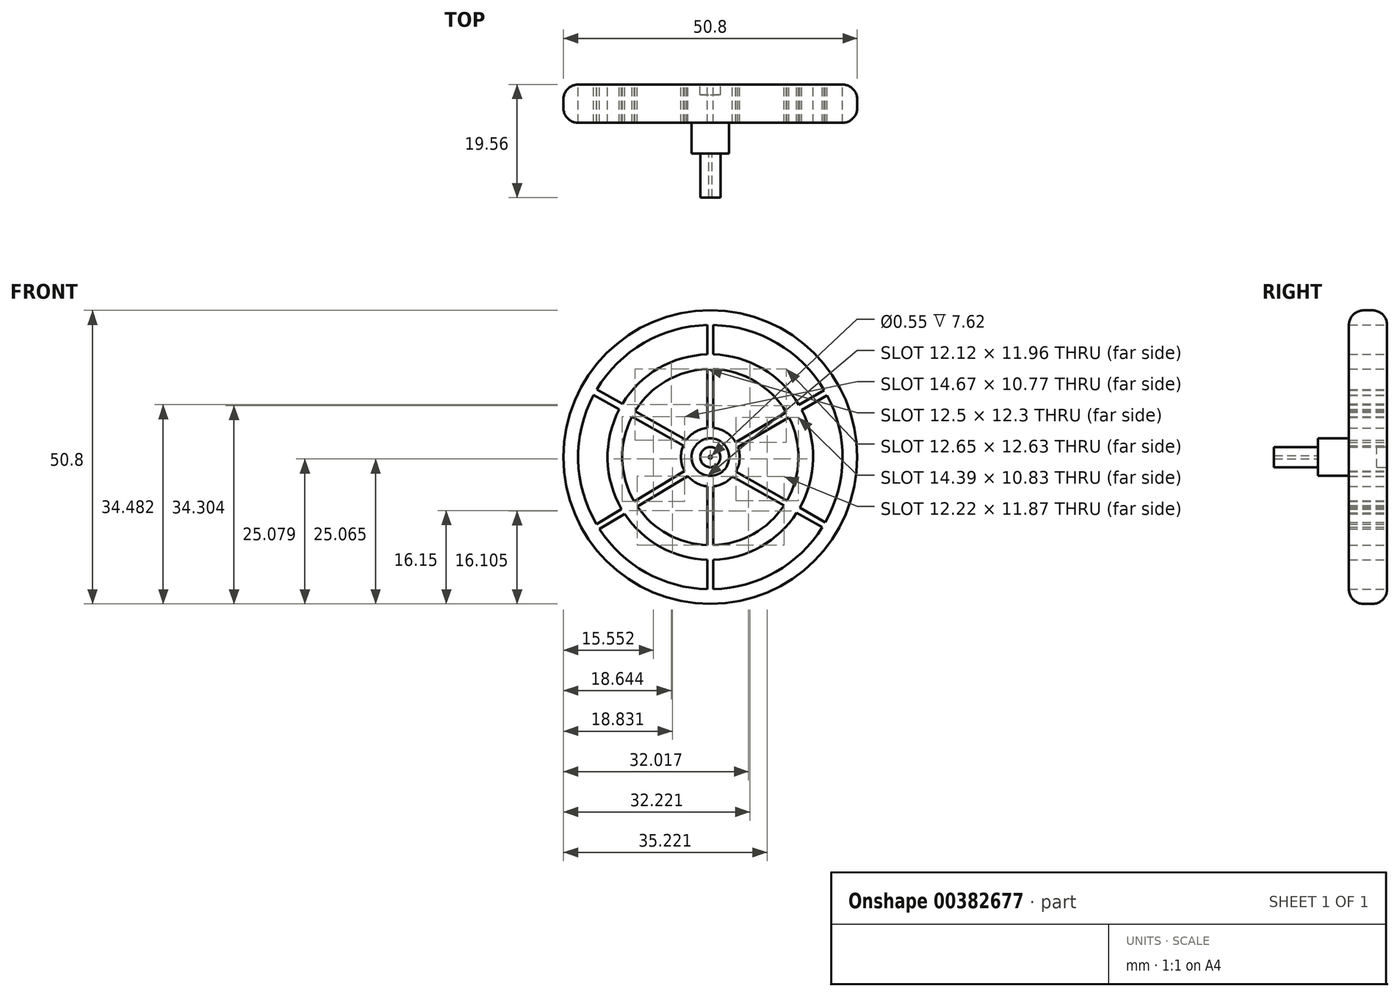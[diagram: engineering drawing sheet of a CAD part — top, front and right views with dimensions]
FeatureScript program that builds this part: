
annotation { "Feature Type Name" : "Feature", "Feature Type Description" : "" }
export const myFeature = defineFeature(function(context is Context, id is Id, definition is map)
    precondition{}
    {
        {
            var Q0;
            Q0=qCreatedBy(makeId("Front.planeOp"),FACE);
            var sketch = newSketch(context, id + "F0", { "sketchPlane" : qUnion([Q0])});
            skCircle(sketch, "E0", {"center": v(0, 0) * mm, "radius": 25.4 * mm});
            skCircle(sketch, "E1", {"center": v(0, 0) * mm, "radius": 22.86 * mm});
            skLineSegment(sketch, "E2", {"start": v(-0.5, 17.77) * mm, "end": v(-0.5, 17.77) * mm});
            skCircle(sketch, "E3", {"center": v(0, 0) * mm, "radius": 5.08 * mm});
            skLineSegment(sketch, "E4", {"start": v(-0.5, 22.85) * mm, "end": v(-0.5, 17.77) * mm});
            skLineSegment(sketch, "E5", {"start": v(0.5, 22.85) * mm, "end": v(0.5, 17.77) * mm});
            skLineSegment(sketch, "E6", {"start": v(-0.5, -5.05) * mm, "end": v(-0.5, -15.23) * mm});
            skLineSegment(sketch, "E7", {"start": v(0.5, -5.05) * mm, "end": v(0.5, -15.23) * mm});
            skLineSegment(sketch, "E8", {"start": v(0.5, 17.77) * mm, "end": v(0.5, 17.77) * mm});
            skArc(sketch, "E9", {"start": v(-0.5, 15.23) * mm, "mid": v(-7.68, 13.17) * mm, "end": v(-13, 7.95) * mm});
            skLineSegment(sketch, "E10", {"start": v(0.5, -15.23) * mm, "end": v(0.5, -15.23) * mm});
            skLineSegment(sketch, "E11", {"start": v(0.5, -17.77) * mm, "end": v(0.5, -22.85) * mm});
            skLineSegment(sketch, "E12", {"start": v(0.5, -17.77) * mm, "end": v(0.5, -17.77) * mm});
            skArc(sketch, "E13.trimOffspring", {"start": v(0.5, -15.23) * mm, "mid": v(7.45, -13.3) * mm, "end": v(12.73, -8.39) * mm});
            skCircle(sketch, "E14", {"center": v(0, 0) * mm, "radius": 1.78 * mm});
            skCircle(sketch, "E15.cCircle", {"center": v(0, 0) * mm, "radius": 22.86 * mm, "construction": true});
            skLineSegment(sketch, "E16", {"start": v(19.7, 11.6) * mm, "end": v(15.32, 9.02) * mm});
            skLineSegment(sketch, "E17", {"start": v(-19.64, 11.7) * mm, "end": v(-15.22, 9.2) * mm});
            skLineSegment(sketch, "E18", {"start": v(4.4, -2.53) * mm, "end": v(13.26, -7.52) * mm});
            skLineSegment(sketch, "E19", {"start": v(-4.46, -2.43) * mm, "end": v(-13.17, -7.67) * mm});
            skLineSegment(sketch, "E20", {"start": v(-4.68, 1.98) * mm, "end": v(-13.54, 7) * mm});
            skArc(sketch, "E21", {"start": v(-15.75, 8.25) * mm, "mid": v(-17.78, -0.37) * mm, "end": v(-15.4, -8.9) * mm});
            skArc(sketch, "E22", {"start": v(-13.54, 7) * mm, "mid": v(-15.24, -0.38) * mm, "end": v(-13.17, -7.67) * mm});
            skLineSegment(sketch, "E23.trimOffspring", {"start": v(-13, 7.95) * mm, "end": v(-4.15, 2.93) * mm});
            skLineSegment(sketch, "E24.trimOffspring", {"start": v(-15.75, 8.25) * mm, "end": v(-20.17, 10.75) * mm});
            skLineSegment(sketch, "E25", {"start": v(4.77, 1.74) * mm, "end": v(13.6, 6.88) * mm});
            skArc(sketch, "E26", {"start": v(15.32, 9.02) * mm, "mid": v(9.04, 15.3) * mm, "end": v(0.5, 17.77) * mm});
            skLineSegment(sketch, "E27", {"start": v(13.13, 7.73) * mm, "end": v(4.38, 2.58) * mm});
            skArc(sketch, "E28", {"start": v(13.13, 7.73) * mm, "mid": v(7.78, 13.1) * mm, "end": v(0.5, 15.23) * mm});
            skLineSegment(sketch, "E29", {"start": v(19.37, -12.13) * mm, "end": v(14.94, -9.64) * mm});
            skLineSegment(sketch, "E30", {"start": v(-3.89, -3.27) * mm, "end": v(-12.63, -8.53) * mm});
            skArc(sketch, "E31", {"start": v(-0.5, 17.77) * mm, "mid": v(-8.96, 15.36) * mm, "end": v(-15.22, 9.2) * mm});
            skLineSegment(sketch, "E32", {"start": v(-0.5, 15.23) * mm, "end": v(-0.5, 5.05) * mm});
            skLineSegment(sketch, "E33", {"start": v(0.5, 15.23) * mm, "end": v(0.5, 5.05) * mm});
            skArc(sketch, "E34", {"start": v(0.5, -17.77) * mm, "mid": v(8.73, -15.49) * mm, "end": v(14.94, -9.64) * mm});
            skLineSegment(sketch, "E35", {"start": v(-0.5, -15.23) * mm, "end": v(-0.5, -15.23) * mm});
            skLineSegment(sketch, "E36", {"start": v(-0.5, -17.77) * mm, "end": v(-0.5, -22.85) * mm});
            skLineSegment(sketch, "E37", {"start": v(-13.17, -7.67) * mm, "end": v(-13.17, -7.67) * mm});
            skArc(sketch, "E38", {"start": v(-15.4, -8.9) * mm, "mid": v(-15.37, -8.94) * mm, "end": v(-15.35, -8.98) * mm});
            skLineSegment(sketch, "E39", {"start": v(-14.8, -9.84) * mm, "end": v(-14.8, -9.84) * mm});
            skLineSegment(sketch, "E40", {"start": v(-14.8, -9.84) * mm, "end": v(-19.17, -12.46) * mm});
            skLineSegment(sketch, "E41.trimOffspring", {"start": v(-15.35, -8.98) * mm, "end": v(-19.7, -11.6) * mm});
            skLineSegment(sketch, "E42", {"start": v(13.13, 7.73) * mm, "end": v(13.13, 7.73) * mm});
            skLineSegment(sketch, "E43", {"start": v(15.8, 8.15) * mm, "end": v(15.8, 8.15) * mm});
            skLineSegment(sketch, "E44", {"start": v(15.8, 8.15) * mm, "end": v(20.2, 10.71) * mm});
            skLineSegment(sketch, "E45", {"start": v(15.47, -8.77) * mm, "end": v(19.9, -11.26) * mm});
            skLineSegment(sketch, "E46", {"start": v(12.76, -8.4) * mm, "end": v(12.55, -8.29) * mm});
            skArc(sketch, "E47", {"start": v(15.47, -8.77) * mm, "mid": v(15.47, -8.76) * mm, "end": v(15.48, -8.74) * mm});
            skLineSegment(sketch, "E48", {"start": v(14.94, -9.64) * mm, "end": v(14.94, -9.64) * mm});
            skArc(sketch, "E49", {"start": v(15.48, -8.74) * mm, "mid": v(17.78, -0.34) * mm, "end": v(15.8, 8.15) * mm});
            skLineSegment(sketch, "E50", {"start": v(13.26, -7.52) * mm, "end": v(13.26, -7.52) * mm});
            skLineSegment(sketch, "E51", {"start": v(12.55, -8.29) * mm, "end": v(3.81, -3.36) * mm});
            skArc(sketch, "E52.trimOffspring", {"start": v(13.26, -7.52) * mm, "mid": v(15.24, -0.36) * mm, "end": v(13.6, 6.88) * mm});
            skArc(sketch, "E53", {"start": v(-12.63, -8.53) * mm, "mid": v(-7.38, -13.34) * mm, "end": v(-0.5, -15.23) * mm});
            skArc(sketch, "E54", {"start": v(-14.8, -9.84) * mm, "mid": v(-8.62, -15.55) * mm, "end": v(-0.5, -17.77) * mm});
            skSolve(sketch);
        }
        {
            var Q0;
            Q0=makeQuery(id+"F0.imprint","IMPRINT",FACE,{"disambiguationData":[TD([[makeQuery(id+"F0.imprint","IMPRINT",EDGE,{"derivedFrom":sQuery(id+"F0.wireOp",EDGE,"E0")}),1.0]])]});
            var Q1;
            {var subQ11=sQuery(id+"F0.wireOp",EDGE,"E6");Q1=makeQuery(id+"F0.imprint","IMPRINT",FACE,{"disambiguationData":[TD([[makeQuery(id+"F0.imprint","IMPRINT",EDGE,{"derivedFrom":subQ11}),1.0]])]});}
            var Q2;
            {var subQ0=sQuery(id+"F0.wireOp",EDGE,"E18");Q2=makeQuery(id+"F0.imprint","IMPRINT",FACE,{"disambiguationData":[TD([[makeQuery(id+"F0.imprint","IMPRINT",EDGE,{"derivedFrom":subQ0}),-1.0]])]});}
            var Q3;
            {var subQ0=sQuery(id+"F0.wireOp",EDGE,"E29");Q3=makeQuery(id+"F0.imprint","IMPRINT",FACE,{"disambiguationData":[TD([[makeQuery(id+"F0.imprint","IMPRINT",EDGE,{"derivedFrom":subQ0}),-1.0]])]});}
            var Q4;
            {var subQ0=sQuery(id+"F0.wireOp",EDGE,"E40");Q4=makeQuery(id+"F0.imprint","IMPRINT",FACE,{"disambiguationData":[TD([[makeQuery(id+"F0.imprint","IMPRINT",EDGE,{"derivedFrom":subQ0}),-1.0]])]});}
            var Q5;
            {var subQ0=sQuery(id+"F0.wireOp",EDGE,"E19");Q5=makeQuery(id+"F0.imprint","IMPRINT",FACE,{"disambiguationData":[TD([[makeQuery(id+"F0.imprint","IMPRINT",EDGE,{"derivedFrom":subQ0}),1.0]])]});}
            var Q6;
            Q6=makeQuery(id+"F0.imprint","IMPRINT",FACE,{"disambiguationData":[TD([[makeQuery(id+"F0.imprint","IMPRINT",EDGE,{"derivedFrom":sQuery(id+"F0.wireOp",EDGE,"E14")}),-1.0]])]});
            extrude(context, id + "F1", {"entities" : qUnion([Q0, Q1, Q2, Q3, Q4, Q5, Q6]), "depth" : 3.56 * mm, "symmetric" : true});
        }
        {
            var Q0;
            Q0 = qSketchRegion(id + "F0", true);
            var Q1;
            Q1=makeQuery(id+"F1.opExtrude","CAP_FACE",FACE,{"disambiguationData":[OSD([sQuery(id+"F0.wireOp",EDGE,"E0"),sQuery(id+"F0.wireOp",EDGE,"E1"),sQuery(id+"F0.wireOp",EDGE,"E3"),sQuery(id+"F0.wireOp",EDGE,"E4"),sQuery(id+"F0.wireOp",EDGE,"E5"),sQuery(id+"F0.wireOp",EDGE,"E6"),sQuery(id+"F0.wireOp",EDGE,"E7"),sQuery(id+"F0.wireOp",EDGE,"E9"),sQuery(id+"F0.wireOp",EDGE,"E11"),sQuery(id+"F0.wireOp",EDGE,"E13.trimOffspring"),sQuery(id+"F0.wireOp",EDGE,"E14"),sQuery(id+"F0.wireOp",EDGE,"E16"),sQuery(id+"F0.wireOp",EDGE,"E17"),sQuery(id+"F0.wireOp",EDGE,"E18"),sQuery(id+"F0.wireOp",EDGE,"E19"),sQuery(id+"F0.wireOp",EDGE,"E20"),sQuery(id+"F0.wireOp",EDGE,"E21"),sQuery(id+"F0.wireOp",EDGE,"E22"),sQuery(id+"F0.wireOp",EDGE,"E23.trimOffspring"),sQuery(id+"F0.wireOp",EDGE,"E24.trimOffspring"),sQuery(id+"F0.wireOp",EDGE,"E25"),sQuery(id+"F0.wireOp",EDGE,"E26"),sQuery(id+"F0.wireOp",EDGE,"E27"),sQuery(id+"F0.wireOp",EDGE,"E28"),sQuery(id+"F0.wireOp",EDGE,"E29"),sQuery(id+"F0.wireOp",EDGE,"E30"),sQuery(id+"F0.wireOp",EDGE,"E31"),sQuery(id+"F0.wireOp",EDGE,"E32"),sQuery(id+"F0.wireOp",EDGE,"E33"),sQuery(id+"F0.wireOp",EDGE,"E34"),sQuery(id+"F0.wireOp",EDGE,"E36"),sQuery(id+"F0.wireOp",EDGE,"E38"),sQuery(id+"F0.wireOp",EDGE,"E40"),sQuery(id+"F0.wireOp",EDGE,"E41.trimOffspring"),sQuery(id+"F0.wireOp",EDGE,"E44"),sQuery(id+"F0.wireOp",EDGE,"E45"),sQuery(id+"F0.wireOp",EDGE,"E46"),sQuery(id+"F0.wireOp",EDGE,"E47"),sQuery(id+"F0.wireOp",EDGE,"E49"),sQuery(id+"F0.wireOp",EDGE,"E51"),sQuery(id+"F0.wireOp",EDGE,"E52.trimOffspring"),sQuery(id+"F0.wireOp",EDGE,"E53"),sQuery(id+"F0.wireOp",EDGE,"E54")])],"isStart":false});
            extrude(context, id + "F2", {"entities" : qUnion([Q0, Q1]), "operationType" : NewBodyOperationType.ADD, "depth" : 3.05 * mm});
        }
        {
            var Q0;
            Q0=qCreatedBy(makeId("Front.planeOp"),FACE);
            var sketch = newSketch(context, id + "F3", { "sketchPlane" : qUnion([Q0])});
            skCircle(sketch, "E55", {"center": v(0, 0) * mm, "radius": 3.25 * mm});
            skSolve(sketch);
        }
        {
            var Q0;
            Q0 = qSketchRegion(id + "F3", true);
            extrude(context, id + "F4", {"entities" : qUnion([Q0]), "operationType" : NewBodyOperationType.ADD, "depth" : 10.16 * mm, "offsetDistance" : 25.4 * mm});
        }
        {
            var Q0;
            Q0=makeQuery(id+"F4.opExtrude","CAP_FACE",FACE,{"disambiguationData":[OSD([sQuery(id+"F3.wireOp",EDGE,"E55")])],"isStart":false});
            var sketch = newSketch(context, id + "F5", { "sketchPlane" : qUnion([Q0])});
            skCircle(sketch, "E56", {"center": v(0, 0) * mm, "radius": 1.74 * mm});
            skCircle(sketch, "E57", {"center": v(0, 0) * mm, "radius": 0.28 * mm});
            skSolve(sketch);
        }
        {
            var Q0;
            Q0=makeQuery(id+"F5.imprint","IMPRINT",FACE,{"disambiguationData":[TD([[makeQuery(id+"F5.imprint","IMPRINT",EDGE,{"derivedFrom":sQuery(id+"F5.wireOp",EDGE,"E56")}),1.0]])]});
            extrude(context, id + "F6", {"entities" : qUnion([Q0]), "operationType" : NewBodyOperationType.ADD, "depth" : 7.62 * mm});
        }
        {
            var Q0;
            Q0=makeQuery(id+"F1.opExtrude","CAP_EDGE",EDGE,{"disambiguationData":[OSD([sQuery(id+"F0.wireOp",EDGE,"E0")])],"isStart":true});
            var Q1;
            {var subQ0=sQuery(id+"F0.wireOp",EDGE,"E0");Q1=makeQuery(id+"F2.opExtrude","CAP_EDGE",EDGE,{"disambiguationData":[OSD([subQ0]),TDD([makeQuery(id+"F1.opExtrude","CAP_EDGE",EDGE,{"disambiguationData":[OSD([subQ0])],"isStart":false})])],"isStart":false});}
            fillet(context, id + "F7", {"entities" : qUnion([Q0, Q1]), "radius" : 2.54 * mm, "tangentPropagation" : true, "allowEdgeOverflow" : false});
        }
    });
